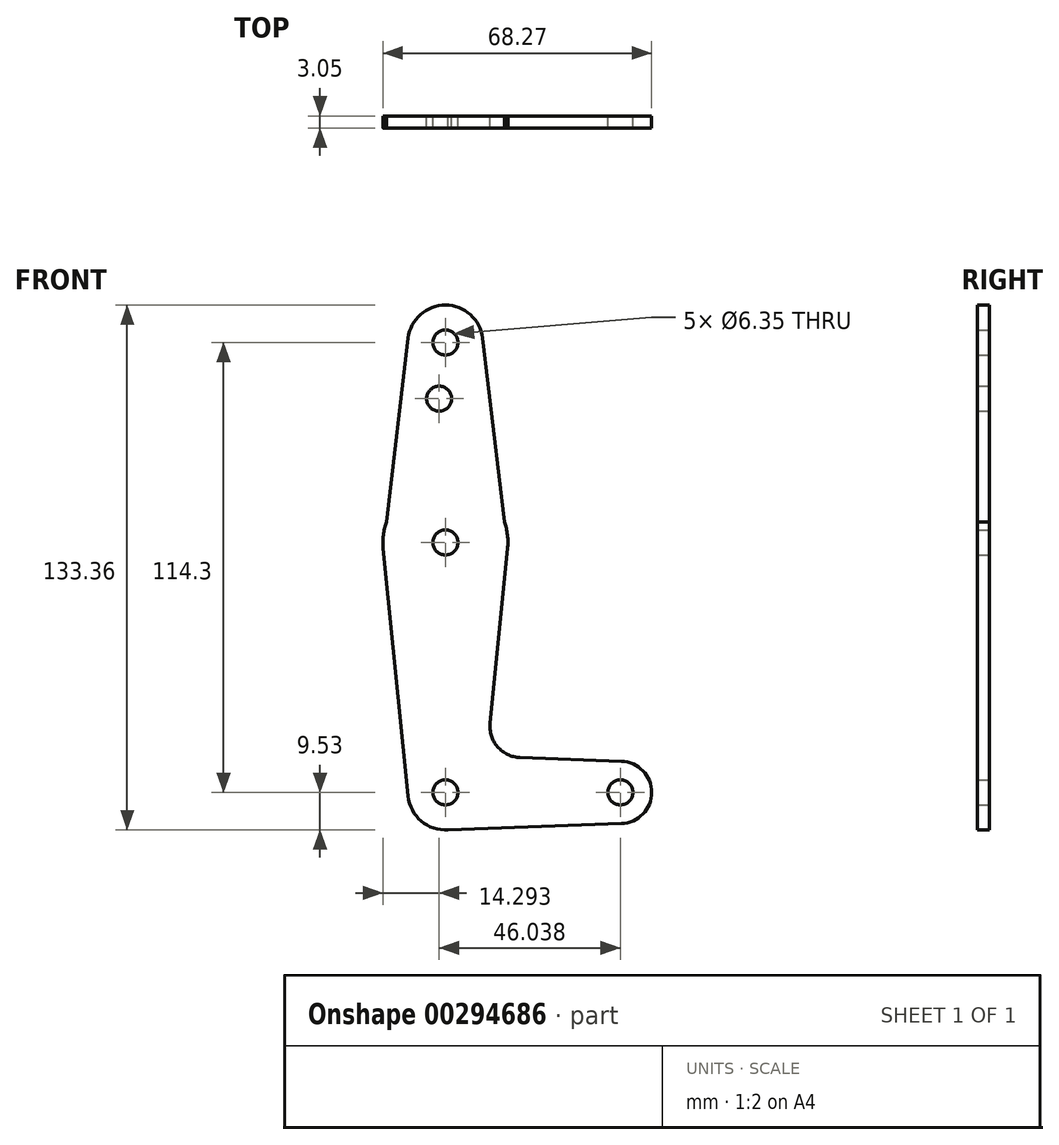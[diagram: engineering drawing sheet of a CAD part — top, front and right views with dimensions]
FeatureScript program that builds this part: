
annotation { "Feature Type Name" : "Feature", "Feature Type Description" : "" }
export const myFeature = defineFeature(function(context is Context, id is Id, definition is map)
    precondition{}
    {
        {
            var Q0;
            Q0=qCreatedBy(makeId("Front.planeOp"),FACE);
            var sketch = newSketch(context, id + "F0", { "sketchPlane" : qUnion([Q0])});
            skCircle(sketch, "E0", {"center": v(0, 0) * mm, "radius": 9.53 * mm});
            skCircle(sketch, "E1", {"center": v(0, 63.5) * mm, "radius": 15.88 * mm});
            skCircle(sketch, "E2", {"center": v(0, 114.3) * mm, "radius": 9.53 * mm});
            skCircle(sketch, "E3", {"center": v(44.45, 0) * mm, "radius": 7.94 * mm});
            skLineSegment(sketch, "E4", {"start": v(0, 0) * mm, "end": v(0, 63.5) * mm, "construction": true});
            skLineSegment(sketch, "E5", {"start": v(0, 63.5) * mm, "end": v(0, 114.3) * mm, "construction": true});
            skLineSegment(sketch, "E6", {"start": v(0, 0) * mm, "end": v(44.45, 0) * mm, "construction": true});
            skLineSegment(sketch, "E7", {"start": v(-15.8, 61.9) * mm, "end": v(-9.46, 115.42) * mm});
            skLineSegment(sketch, "E8", {"start": v(15.8, 61.9) * mm, "end": v(9.46, 115.42) * mm});
            skLineSegment(sketch, "E9", {"start": v(0, -9.53) * mm, "end": v(44.73, -7.93) * mm});
            skCircle(sketch, "E10", {"center": v(0, 114.3) * mm, "radius": 3.18 * mm});
            skCircle(sketch, "E11", {"center": v(-1.59, 100.03) * mm, "radius": 3.18 * mm});
            skCircle(sketch, "E12", {"center": v(0, 63.5) * mm, "radius": 3.17 * mm});
            skCircle(sketch, "E13", {"center": v(0, 0) * mm, "radius": 3.18 * mm});
            skCircle(sketch, "E14", {"center": v(44.45, 0) * mm, "radius": 3.18 * mm});
            skPoint(sketch, "E15.newPointA", {"position": v(0, 9.53) * mm});
            skLineSegment(sketch, "E16", {"start": v(-15.8, 61.91) * mm, "end": v(-9.48, -0.95) * mm});
            skLineSegment(sketch, "E17", {"start": v(-9.48, -0.95) * mm, "end": v(-12, 24.18) * mm});
            skLineSegment(sketch, "E18", {"start": v(15.8, 61.91) * mm, "end": v(11.34, 17.6) * mm});
            skLineSegment(sketch, "E19", {"start": v(18.97, 8.85) * mm, "end": v(44.73, 7.93) * mm});
            skArc(sketch, "E20.filletArc", {"start": v(11.34, 17.6) * mm, "mid": v(13.26, 11.57) * mm, "end": v(18.97, 8.85) * mm});
            skSolve(sketch);
        }
        {
            var Q0;
            Q0 = qSketchRegion(id + "F0", true);
            extrude(context, id + "F1", {"entities" : qUnion([Q0]), "depth" : 3.05 * mm});
        }
    });
